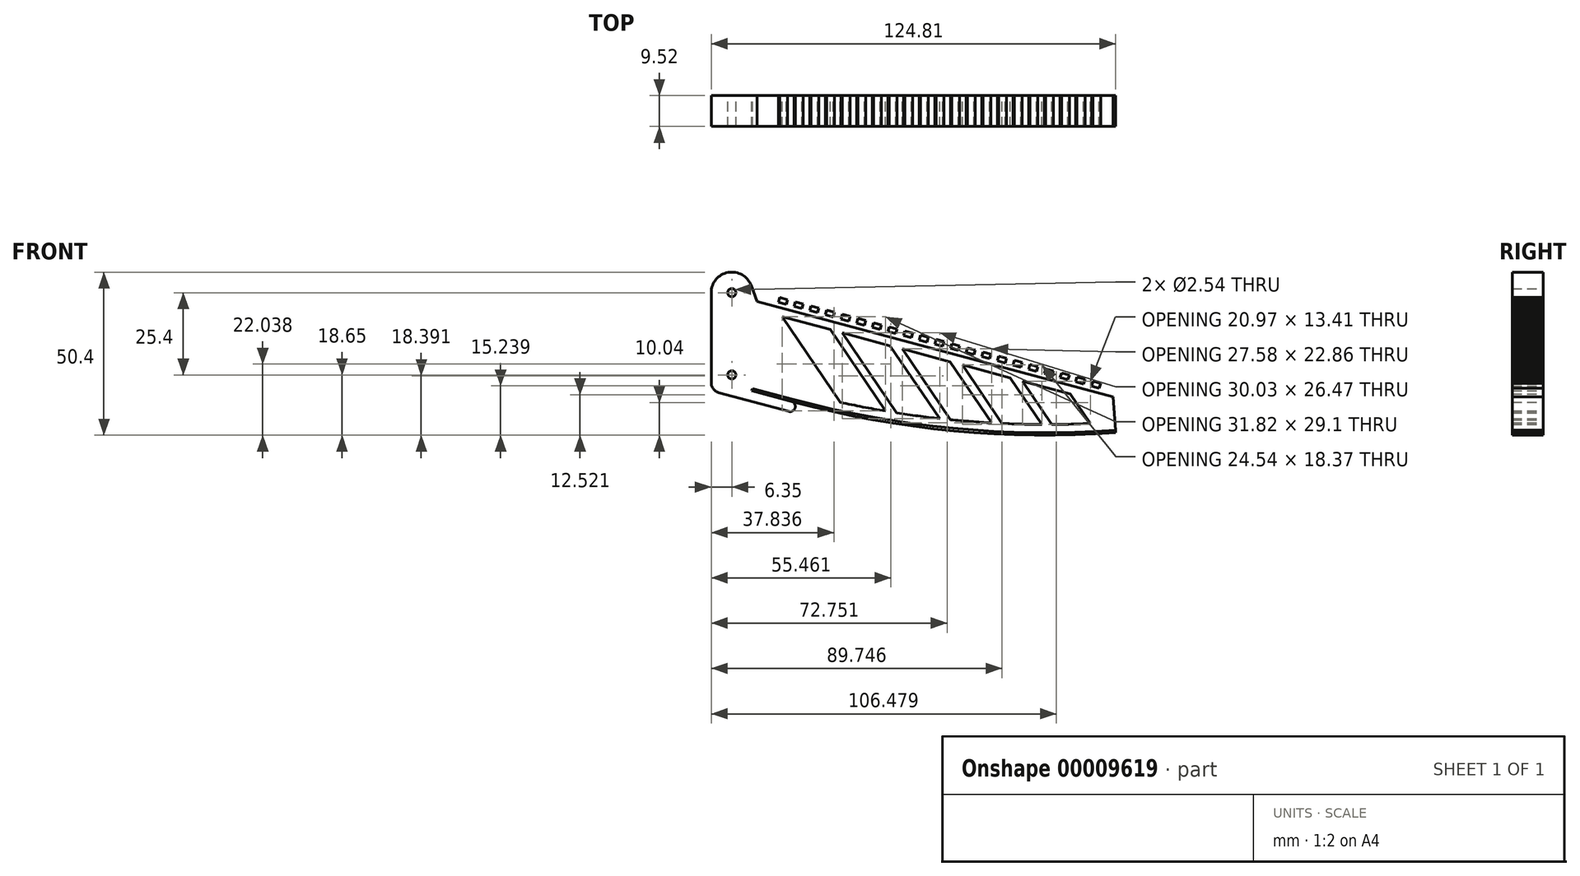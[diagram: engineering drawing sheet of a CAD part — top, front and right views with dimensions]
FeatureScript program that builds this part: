
annotation { "Feature Type Name" : "Feature", "Feature Type Description" : "" }
export const myFeature = defineFeature(function(context is Context, id is Id, definition is map)
    precondition{}
    {
        {
            var Q0;
            Q0=qCreatedBy(makeId("Front.planeOp"),FACE);
            var sketch = newSketch(context, id + "F0", { "sketchPlane" : qUnion([Q0])});
            skCircle(sketch, "E0", {"center": v(0, 0) * mm, "radius": 1.27 * mm});
            skCircle(sketch, "E1", {"center": v(0, 25.4) * mm, "radius": 1.27 * mm});
            skArc(sketch, "E2", {"start": v(5.96, 27.6) * mm, "mid": v(-1.11, 31.65) * mm, "end": v(-6.35, 25.4) * mm});
            skLineSegment(sketch, "E3", {"start": v(-6.35, 25.4) * mm, "end": v(-6.35, -2.44) * mm});
            skLineSegment(sketch, "E4", {"start": v(-4, -5.5) * mm, "end": v(17.58, -11.28) * mm});
            skLineSegment(sketch, "E5", {"start": v(19.48, -9.2) * mm, "end": v(5.96, 27.6) * mm});
            skLineSegment(sketch, "E6", {"start": v(7.14, 24.38) * mm, "end": v(117.54, -5.2) * mm});
            skLineSegment(sketch, "E7", {"start": v(117.54, -5.2) * mm, "end": v(118.46, -17.87) * mm});
            skPoint(sketch, "E8.visualSharp", {"position": v(-6.35, -4.87) * mm});
            skArc(sketch, "E8.filletArc", {"start": v(-6.35, -2.44) * mm, "mid": v(-5.7, -4.37) * mm, "end": v(-4, -5.5) * mm});
            skArc(sketch, "E9", {"start": v(19.2, -8.43) * mm, "mid": v(68.43, -17.3) * mm, "end": v(118.46, -17.87) * mm});
            skLineSegment(sketch, "E10", {"start": v(19.2, -8.43) * mm, "end": v(6.16, -4.94) * mm});
            skLineSegment(sketch, "E11", {"start": v(6.16, -4.94) * mm, "end": v(6.36, -4.2) * mm});
            skLineSegment(sketch, "E12", {"start": v(6.36, -4.2) * mm, "end": v(18.88, -7.56) * mm});
            skArc(sketch, "E13", {"start": v(18.88, -7.56) * mm, "mid": v(68.24, -16.47) * mm, "end": v(118.4, -17.1) * mm});
            skLineSegment(sketch, "E14", {"start": v(118.46, -17.87) * mm, "end": v(126.17, -17.3) * mm, "construction": true});
            skPoint(sketch, "E15.visualSharp", {"position": v(20.54, -12.08) * mm});
            skArc(sketch, "E15.filletArc", {"start": v(17.58, -11.28) * mm, "mid": v(19.16, -10.82) * mm, "end": v(19.48, -9.2) * mm});
            skLineSegment(sketch, "E16.bottom", {"start": v(9.55, 23.74) * mm, "end": v(11.97, 23.09) * mm});
            skLineSegment(sketch, "E16.top", {"start": v(9.94, 25.18) * mm, "end": v(12.36, 24.54) * mm});
            skLineSegment(sketch, "E16.left", {"start": v(9.55, 23.74) * mm, "end": v(9.94, 25.18) * mm});
            skLineSegment(sketch, "E16.right", {"start": v(11.97, 23.09) * mm, "end": v(12.36, 24.54) * mm});
            skLineSegment(sketch, "E17.1.0.0", {"start": v(14.38, 22.44) * mm, "end": v(14.77, 23.9) * mm});
            skLineSegment(sketch, "E17.1.0.1", {"start": v(16.8, 21.8) * mm, "end": v(17.19, 23.24) * mm});
            skLineSegment(sketch, "E17.1.0.2", {"start": v(14.77, 23.9) * mm, "end": v(17.19, 23.24) * mm});
            skLineSegment(sketch, "E17.1.0.3", {"start": v(14.38, 22.44) * mm, "end": v(16.8, 21.8) * mm});
            skLineSegment(sketch, "E17.2.0.0", {"start": v(19.21, 21.15) * mm, "end": v(19.6, 22.6) * mm});
            skLineSegment(sketch, "E17.2.0.1", {"start": v(21.63, 20.5) * mm, "end": v(22.02, 21.95) * mm});
            skLineSegment(sketch, "E17.2.0.2", {"start": v(19.6, 22.6) * mm, "end": v(22.02, 21.95) * mm});
            skLineSegment(sketch, "E17.2.0.3", {"start": v(19.21, 21.15) * mm, "end": v(21.63, 20.5) * mm});
            skLineSegment(sketch, "E17.3.0.0", {"start": v(24.04, 19.85) * mm, "end": v(24.43, 21.3) * mm});
            skLineSegment(sketch, "E17.3.0.1", {"start": v(26.46, 19.2) * mm, "end": v(26.85, 20.66) * mm});
            skLineSegment(sketch, "E17.3.0.2", {"start": v(24.43, 21.3) * mm, "end": v(26.85, 20.66) * mm});
            skLineSegment(sketch, "E17.3.0.3", {"start": v(24.04, 19.85) * mm, "end": v(26.46, 19.2) * mm});
            skLineSegment(sketch, "E17.4.0.0", {"start": v(28.87, 18.56) * mm, "end": v(29.26, 20) * mm});
            skLineSegment(sketch, "E17.4.0.1", {"start": v(31.29, 17.91) * mm, "end": v(31.68, 19.36) * mm});
            skLineSegment(sketch, "E17.4.0.2", {"start": v(29.26, 20) * mm, "end": v(31.68, 19.36) * mm});
            skLineSegment(sketch, "E17.4.0.3", {"start": v(28.87, 18.56) * mm, "end": v(31.29, 17.91) * mm});
            skLineSegment(sketch, "E17.5.0.0", {"start": v(33.7, 17.27) * mm, "end": v(34.1, 18.71) * mm});
            skLineSegment(sketch, "E17.5.0.1", {"start": v(36.12, 16.62) * mm, "end": v(36.5, 18.07) * mm});
            skLineSegment(sketch, "E17.5.0.2", {"start": v(34.1, 18.71) * mm, "end": v(36.5, 18.07) * mm});
            skLineSegment(sketch, "E17.5.0.3", {"start": v(33.7, 17.27) * mm, "end": v(36.12, 16.62) * mm});
            skLineSegment(sketch, "E17.6.0.0", {"start": v(38.53, 15.97) * mm, "end": v(38.92, 17.42) * mm});
            skLineSegment(sketch, "E17.6.0.1", {"start": v(40.95, 15.32) * mm, "end": v(41.33, 16.77) * mm});
            skLineSegment(sketch, "E17.6.0.2", {"start": v(38.92, 17.42) * mm, "end": v(41.33, 16.77) * mm});
            skLineSegment(sketch, "E17.6.0.3", {"start": v(38.53, 15.97) * mm, "end": v(40.95, 15.32) * mm});
            skLineSegment(sketch, "E17.7.0.0", {"start": v(43.36, 14.68) * mm, "end": v(43.75, 16.13) * mm});
            skLineSegment(sketch, "E17.7.0.1", {"start": v(45.78, 14.03) * mm, "end": v(46.16, 15.48) * mm});
            skLineSegment(sketch, "E17.7.0.2", {"start": v(43.75, 16.13) * mm, "end": v(46.16, 15.48) * mm});
            skLineSegment(sketch, "E17.7.0.3", {"start": v(43.36, 14.68) * mm, "end": v(45.78, 14.03) * mm});
            skLineSegment(sketch, "E17.8.0.0", {"start": v(48.2, 13.38) * mm, "end": v(48.58, 14.83) * mm});
            skLineSegment(sketch, "E17.8.0.1", {"start": v(50.6, 12.74) * mm, "end": v(51, 14.19) * mm});
            skLineSegment(sketch, "E17.8.0.2", {"start": v(48.58, 14.83) * mm, "end": v(51, 14.19) * mm});
            skLineSegment(sketch, "E17.8.0.3", {"start": v(48.2, 13.38) * mm, "end": v(50.6, 12.74) * mm});
            skLineSegment(sketch, "E17.9.0.0", {"start": v(53.02, 12.09) * mm, "end": v(53.4, 13.54) * mm});
            skLineSegment(sketch, "E17.9.0.1", {"start": v(55.44, 11.44) * mm, "end": v(55.82, 12.9) * mm});
            skLineSegment(sketch, "E17.9.0.2", {"start": v(53.4, 13.54) * mm, "end": v(55.82, 12.9) * mm});
            skLineSegment(sketch, "E17.9.0.3", {"start": v(53.02, 12.09) * mm, "end": v(55.44, 11.44) * mm});
            skLineSegment(sketch, "E17.10.0.0", {"start": v(57.85, 10.8) * mm, "end": v(58.24, 12.24) * mm});
            skLineSegment(sketch, "E17.10.0.1", {"start": v(60.26, 10.15) * mm, "end": v(60.65, 11.6) * mm});
            skLineSegment(sketch, "E17.10.0.2", {"start": v(58.24, 12.24) * mm, "end": v(60.65, 11.6) * mm});
            skLineSegment(sketch, "E17.10.0.3", {"start": v(57.85, 10.8) * mm, "end": v(60.26, 10.15) * mm});
            skLineSegment(sketch, "E17.11.0.0", {"start": v(62.68, 9.5) * mm, "end": v(63.07, 10.95) * mm});
            skLineSegment(sketch, "E17.11.0.1", {"start": v(65.1, 8.85) * mm, "end": v(65.48, 10.3) * mm});
            skLineSegment(sketch, "E17.11.0.2", {"start": v(63.07, 10.95) * mm, "end": v(65.48, 10.3) * mm});
            skLineSegment(sketch, "E17.11.0.3", {"start": v(62.68, 9.5) * mm, "end": v(65.1, 8.85) * mm});
            skLineSegment(sketch, "E17.12.0.0", {"start": v(67.5, 8.2) * mm, "end": v(67.9, 9.66) * mm});
            skLineSegment(sketch, "E17.12.0.1", {"start": v(69.92, 7.56) * mm, "end": v(70.31, 9) * mm});
            skLineSegment(sketch, "E17.12.0.2", {"start": v(67.9, 9.66) * mm, "end": v(70.31, 9) * mm});
            skLineSegment(sketch, "E17.12.0.3", {"start": v(67.5, 8.2) * mm, "end": v(69.92, 7.56) * mm});
            skLineSegment(sketch, "E17.13.0.0", {"start": v(72.34, 6.91) * mm, "end": v(72.73, 8.36) * mm});
            skLineSegment(sketch, "E17.13.0.1", {"start": v(74.75, 6.27) * mm, "end": v(75.14, 7.71) * mm});
            skLineSegment(sketch, "E17.13.0.2", {"start": v(72.73, 8.36) * mm, "end": v(75.14, 7.71) * mm});
            skLineSegment(sketch, "E17.13.0.3", {"start": v(72.34, 6.91) * mm, "end": v(74.75, 6.27) * mm});
            skLineSegment(sketch, "E17.14.0.0", {"start": v(77.17, 5.62) * mm, "end": v(77.56, 7.07) * mm});
            skLineSegment(sketch, "E17.14.0.1", {"start": v(79.58, 4.97) * mm, "end": v(79.97, 6.42) * mm});
            skLineSegment(sketch, "E17.14.0.2", {"start": v(77.56, 7.07) * mm, "end": v(79.97, 6.42) * mm});
            skLineSegment(sketch, "E17.14.0.3", {"start": v(77.17, 5.62) * mm, "end": v(79.58, 4.97) * mm});
            skLineSegment(sketch, "E17.15.0.0", {"start": v(82, 4.32) * mm, "end": v(82.39, 5.77) * mm});
            skLineSegment(sketch, "E17.15.0.1", {"start": v(84.41, 3.68) * mm, "end": v(84.8, 5.13) * mm});
            skLineSegment(sketch, "E17.15.0.2", {"start": v(82.39, 5.77) * mm, "end": v(84.8, 5.13) * mm});
            skLineSegment(sketch, "E17.15.0.3", {"start": v(82, 4.32) * mm, "end": v(84.41, 3.68) * mm});
            skLineSegment(sketch, "E17.16.0.0", {"start": v(86.83, 3.03) * mm, "end": v(87.22, 4.48) * mm});
            skLineSegment(sketch, "E17.16.0.1", {"start": v(89.24, 2.38) * mm, "end": v(89.63, 3.83) * mm});
            skLineSegment(sketch, "E17.16.0.2", {"start": v(87.22, 4.48) * mm, "end": v(89.63, 3.83) * mm});
            skLineSegment(sketch, "E17.16.0.3", {"start": v(86.83, 3.03) * mm, "end": v(89.24, 2.38) * mm});
            skLineSegment(sketch, "E17.17.0.0", {"start": v(91.66, 1.74) * mm, "end": v(92.05, 3.19) * mm});
            skLineSegment(sketch, "E17.17.0.1", {"start": v(94.07, 1.09) * mm, "end": v(94.46, 2.54) * mm});
            skLineSegment(sketch, "E17.17.0.2", {"start": v(92.05, 3.19) * mm, "end": v(94.46, 2.54) * mm});
            skLineSegment(sketch, "E17.17.0.3", {"start": v(91.66, 1.74) * mm, "end": v(94.07, 1.09) * mm});
            skLineSegment(sketch, "E17.18.0.0", {"start": v(96.49, 0.44) * mm, "end": v(96.88, 1.9) * mm});
            skLineSegment(sketch, "E17.18.0.1", {"start": v(98.9, -0.2) * mm, "end": v(99.3, 1.24) * mm});
            skLineSegment(sketch, "E17.18.0.2", {"start": v(96.88, 1.9) * mm, "end": v(99.3, 1.24) * mm});
            skLineSegment(sketch, "E17.18.0.3", {"start": v(96.49, 0.44) * mm, "end": v(98.9, -0.2) * mm});
            skLineSegment(sketch, "E17.19.0.0", {"start": v(101.32, -0.85) * mm, "end": v(101.7, 0.6) * mm});
            skLineSegment(sketch, "E17.19.0.1", {"start": v(103.73, -1.5) * mm, "end": v(104.12, -0.05) * mm});
            skLineSegment(sketch, "E17.19.0.2", {"start": v(101.7, 0.6) * mm, "end": v(104.12, -0.05) * mm});
            skLineSegment(sketch, "E17.19.0.3", {"start": v(101.32, -0.85) * mm, "end": v(103.73, -1.5) * mm});
            skLineSegment(sketch, "E17.direction1", {"start": v(9.55, 23.74) * mm, "end": v(14.38, 22.44) * mm, "construction": true});
            skLineSegment(sketch, "E18.0.20.0", {"start": v(106.15, -2.15) * mm, "end": v(106.53, -0.7) * mm});
            skLineSegment(sketch, "E18.3.20.0", {"start": v(108.56, -2.8) * mm, "end": v(108.95, -1.34) * mm});
            skLineSegment(sketch, "E18.6.20.0", {"start": v(106.53, -0.7) * mm, "end": v(108.95, -1.34) * mm});
            skLineSegment(sketch, "E18.9.20.0", {"start": v(106.15, -2.15) * mm, "end": v(108.56, -2.8) * mm});
            skLineSegment(sketch, "E18.0.21.0", {"start": v(110.98, -3.44) * mm, "end": v(111.36, -2) * mm});
            skLineSegment(sketch, "E18.3.21.0", {"start": v(113.4, -4.09) * mm, "end": v(113.78, -2.64) * mm});
            skLineSegment(sketch, "E18.6.21.0", {"start": v(111.36, -2) * mm, "end": v(113.78, -2.64) * mm});
            skLineSegment(sketch, "E18.9.21.0", {"start": v(110.98, -3.44) * mm, "end": v(113.4, -4.09) * mm});
            skLineSegment(sketch, "E19", {"start": v(117.66, -6.78) * mm, "end": v(7.77, 22.66) * mm});
            skArc(sketch, "E20", {"start": v(17.8, -4.63) * mm, "mid": v(67.6, -13.86) * mm, "end": v(118.22, -14.57) * mm, "construction": true});
            skLineSegment(sketch, "E21", {"start": v(110.61, -15.01) * mm, "end": v(104.41, -5.86) * mm});
            skLineSegment(sketch, "E22", {"start": v(104.41, -5.86) * mm, "end": v(89.64, -1.9) * mm});
            skLineSegment(sketch, "E23", {"start": v(89.64, -1.9) * mm, "end": v(98.73, -15.31) * mm});
            skArc(sketch, "E24", {"start": v(98.73, -15.31) * mm, "mid": v(104.68, -15.22) * mm, "end": v(110.61, -15.01) * mm});
            skLineSegment(sketch, "E25", {"start": v(95.67, -15.31) * mm, "end": v(85.9, -0.9) * mm});
            skLineSegment(sketch, "E26", {"start": v(71.13, 3.06) * mm, "end": v(83.37, -15) * mm});
            skLineSegment(sketch, "E27", {"start": v(71.13, 3.06) * mm, "end": v(85.9, -0.9) * mm});
            skLineSegment(sketch, "E28", {"start": v(80.2, -14.84) * mm, "end": v(67.38, 4.06) * mm});
            skLineSegment(sketch, "E29", {"start": v(67.38, 4.06) * mm, "end": v(52.61, 8.02) * mm});
            skLineSegment(sketch, "E30", {"start": v(52.61, 8.02) * mm, "end": v(67.43, -13.84) * mm});
            skLineSegment(sketch, "E31", {"start": v(64.13, -13.5) * mm, "end": v(48.86, 9.02) * mm});
            skLineSegment(sketch, "E32", {"start": v(48.86, 9.02) * mm, "end": v(34.1, 12.98) * mm});
            skLineSegment(sketch, "E33", {"start": v(34.1, 12.98) * mm, "end": v(50.84, -11.72) * mm});
            skLineSegment(sketch, "E34", {"start": v(47.4, -11.16) * mm, "end": v(30.34, 13.98) * mm});
            skLineSegment(sketch, "E35", {"start": v(30.34, 13.98) * mm, "end": v(15.58, 17.94) * mm});
            skLineSegment(sketch, "E36", {"start": v(15.58, 17.94) * mm, "end": v(33.5, -8.49) * mm});
            skLineSegment(sketch, "E37", {"start": v(85.9, -0.9) * mm, "end": v(89.64, -1.9) * mm, "construction": true});
            skLineSegment(sketch, "E38", {"start": v(71.13, 3.06) * mm, "end": v(67.38, 4.06) * mm, "construction": true});
            skLineSegment(sketch, "E39", {"start": v(52.61, 8.02) * mm, "end": v(48.86, 9.02) * mm, "construction": true});
            skLineSegment(sketch, "E40", {"start": v(34.1, 12.98) * mm, "end": v(30.34, 13.98) * mm, "construction": true});
            skArc(sketch, "E41", {"start": v(83.37, -15) * mm, "mid": v(89.52, -15.22) * mm, "end": v(95.67, -15.31) * mm});
            skArc(sketch, "E42", {"start": v(67.43, -13.84) * mm, "mid": v(73.8, -14.4) * mm, "end": v(80.2, -14.84) * mm});
            skArc(sketch, "E43", {"start": v(50.84, -11.72) * mm, "mid": v(57.48, -12.68) * mm, "end": v(64.13, -13.5) * mm});
            skArc(sketch, "E44", {"start": v(33.5, -8.49) * mm, "mid": v(40.43, -9.9) * mm, "end": v(47.4, -11.16) * mm});
            skArc(sketch, "E45", {"start": v(10.98, 13.93) * mm, "mid": v(1.57, 6.41) * mm, "end": v(13.6, 6.78) * mm});
            skSolve(sketch);
        }
        {
            var Q0;
            Q0=makeQuery(id+"F0.imprint","IMPRINT",FACE,{"disambiguationData":[TD([[makeQuery(id+"F0.imprint","IMPRINT",EDGE,{"derivedFrom":sQuery(id+"F0.wireOp",EDGE,"E0")}),-1.0]])]});
            var Q1;
            {var subQ0=sQuery(id+"F0.wireOp",EDGE,"E45");Q1=makeQuery(id+"F0.imprint","IMPRINT",FACE,{"disambiguationData":[TD([[makeQuery(id+"F0.imprint","IMPRINT",EDGE,{"derivedFrom":subQ0}),1.0]])]});}
            extrude(context, id + "F1", {"entities" : qUnion([Q0, Q1]), "depth" : 9.52 * mm, "symmetric" : true});
        }
        {
            var Q0;
            {var subQ22=sQuery(id+"F0.wireOp",EDGE,"E16.bottom");Q0=makeQuery(id+"F0.imprint","IMPRINT",FACE,{"disambiguationData":[TD([[makeQuery(id+"F0.imprint","IMPRINT",EDGE,{"derivedFrom":subQ22}),-1.0]])]});}
            var Q1;
            Q1=makeQuery(id+"F0.imprint","IMPRINT",FACE,{"disambiguationData":[TD([[makeQuery(id+"F0.imprint","IMPRINT",EDGE,{"derivedFrom":sQuery(id+"F0.wireOp",EDGE,"E16.bottom")}),1.0]])]});
            var Q2;
            Q2=makeQuery(id+"F0.imprint","IMPRINT",FACE,{"disambiguationData":[TD([[makeQuery(id+"F0.imprint","IMPRINT",EDGE,{"derivedFrom":sQuery(id+"F0.wireOp",EDGE,"E17.1.0.0")}),-1.0]])]});
            var Q3;
            Q3=makeQuery(id+"F0.imprint","IMPRINT",FACE,{"disambiguationData":[TD([[makeQuery(id+"F0.imprint","IMPRINT",EDGE,{"derivedFrom":sQuery(id+"F0.wireOp",EDGE,"E17.2.0.0")}),-1.0]])]});
            var Q4;
            Q4=makeQuery(id+"F0.imprint","IMPRINT",FACE,{"disambiguationData":[TD([[makeQuery(id+"F0.imprint","IMPRINT",EDGE,{"derivedFrom":sQuery(id+"F0.wireOp",EDGE,"E17.3.0.0")}),-1.0]])]});
            var Q5;
            Q5=makeQuery(id+"F0.imprint","IMPRINT",FACE,{"disambiguationData":[TD([[makeQuery(id+"F0.imprint","IMPRINT",EDGE,{"derivedFrom":sQuery(id+"F0.wireOp",EDGE,"E17.4.0.0")}),-1.0]])]});
            var Q6;
            Q6=makeQuery(id+"F0.imprint","IMPRINT",FACE,{"disambiguationData":[TD([[makeQuery(id+"F0.imprint","IMPRINT",EDGE,{"derivedFrom":sQuery(id+"F0.wireOp",EDGE,"E17.5.0.0")}),-1.0]])]});
            var Q7;
            Q7=makeQuery(id+"F0.imprint","IMPRINT",FACE,{"disambiguationData":[TD([[makeQuery(id+"F0.imprint","IMPRINT",EDGE,{"derivedFrom":sQuery(id+"F0.wireOp",EDGE,"E17.6.0.0")}),-1.0]])]});
            var Q8;
            Q8=makeQuery(id+"F0.imprint","IMPRINT",FACE,{"disambiguationData":[TD([[makeQuery(id+"F0.imprint","IMPRINT",EDGE,{"derivedFrom":sQuery(id+"F0.wireOp",EDGE,"E17.7.0.0")}),-1.0]])]});
            var Q9;
            Q9=makeQuery(id+"F0.imprint","IMPRINT",FACE,{"disambiguationData":[TD([[makeQuery(id+"F0.imprint","IMPRINT",EDGE,{"derivedFrom":sQuery(id+"F0.wireOp",EDGE,"E17.8.0.0")}),-1.0]])]});
            var Q10;
            Q10=makeQuery(id+"F0.imprint","IMPRINT",FACE,{"disambiguationData":[TD([[makeQuery(id+"F0.imprint","IMPRINT",EDGE,{"derivedFrom":sQuery(id+"F0.wireOp",EDGE,"E17.9.0.0")}),-1.0]])]});
            var Q11;
            Q11=makeQuery(id+"F0.imprint","IMPRINT",FACE,{"disambiguationData":[TD([[makeQuery(id+"F0.imprint","IMPRINT",EDGE,{"derivedFrom":sQuery(id+"F0.wireOp",EDGE,"E17.10.0.0")}),-1.0]])]});
            var Q12;
            Q12=makeQuery(id+"F0.imprint","IMPRINT",FACE,{"disambiguationData":[TD([[makeQuery(id+"F0.imprint","IMPRINT",EDGE,{"derivedFrom":sQuery(id+"F0.wireOp",EDGE,"E17.11.0.0")}),-1.0]])]});
            var Q13;
            Q13=makeQuery(id+"F0.imprint","IMPRINT",FACE,{"disambiguationData":[TD([[makeQuery(id+"F0.imprint","IMPRINT",EDGE,{"derivedFrom":sQuery(id+"F0.wireOp",EDGE,"E17.12.0.0")}),-1.0]])]});
            var Q14;
            Q14=makeQuery(id+"F0.imprint","IMPRINT",FACE,{"disambiguationData":[TD([[makeQuery(id+"F0.imprint","IMPRINT",EDGE,{"derivedFrom":sQuery(id+"F0.wireOp",EDGE,"E17.13.0.0")}),-1.0]])]});
            var Q15;
            Q15=makeQuery(id+"F0.imprint","IMPRINT",FACE,{"disambiguationData":[TD([[makeQuery(id+"F0.imprint","IMPRINT",EDGE,{"derivedFrom":sQuery(id+"F0.wireOp",EDGE,"E17.14.0.0")}),-1.0]])]});
            var Q16;
            Q16=makeQuery(id+"F0.imprint","IMPRINT",FACE,{"disambiguationData":[TD([[makeQuery(id+"F0.imprint","IMPRINT",EDGE,{"derivedFrom":sQuery(id+"F0.wireOp",EDGE,"E17.15.0.0")}),-1.0]])]});
            var Q17;
            Q17=makeQuery(id+"F0.imprint","IMPRINT",FACE,{"disambiguationData":[TD([[makeQuery(id+"F0.imprint","IMPRINT",EDGE,{"derivedFrom":sQuery(id+"F0.wireOp",EDGE,"E17.16.0.0")}),-1.0]])]});
            var Q18;
            Q18=makeQuery(id+"F0.imprint","IMPRINT",FACE,{"disambiguationData":[TD([[makeQuery(id+"F0.imprint","IMPRINT",EDGE,{"derivedFrom":sQuery(id+"F0.wireOp",EDGE,"E17.17.0.0")}),-1.0]])]});
            var Q19;
            Q19=makeQuery(id+"F0.imprint","IMPRINT",FACE,{"disambiguationData":[TD([[makeQuery(id+"F0.imprint","IMPRINT",EDGE,{"derivedFrom":sQuery(id+"F0.wireOp",EDGE,"E17.18.0.0")}),-1.0]])]});
            var Q20;
            Q20=makeQuery(id+"F0.imprint","IMPRINT",FACE,{"disambiguationData":[TD([[makeQuery(id+"F0.imprint","IMPRINT",EDGE,{"derivedFrom":sQuery(id+"F0.wireOp",EDGE,"E18.0.20.0")}),-1.0]])]});
            var Q21;
            Q21=makeQuery(id+"F0.imprint","IMPRINT",FACE,{"disambiguationData":[TD([[makeQuery(id+"F0.imprint","IMPRINT",EDGE,{"derivedFrom":sQuery(id+"F0.wireOp",EDGE,"E18.0.21.0")}),-1.0]])]});
            var Q22;
            Q22=makeQuery(id+"F0.imprint","IMPRINT",FACE,{"disambiguationData":[TD([[makeQuery(id+"F0.imprint","IMPRINT",EDGE,{"derivedFrom":sQuery(id+"F0.wireOp",EDGE,"E17.19.0.0")}),-1.0]])]});
            extrude(context, id + "F2", {"entities" : qUnion([Q0, Q1, Q2, Q3, Q4, Q5, Q6, Q7, Q8, Q9, Q10, Q11, Q12, Q13, Q14, Q15, Q16, Q17, Q18, Q19, Q20, Q21, Q22]), "depth" : 9.52 * mm, "symmetric" : true});
        }
        {
            var Q0;
            {var subQ5=sQuery(id+"F0.wireOp",EDGE,"E13");Q0=makeQuery(id+"F0.imprint","IMPRINT",FACE,{"disambiguationData":[TD([[makeQuery(id+"F0.imprint","IMPRINT",EDGE,{"derivedFrom":subQ5}),1.0]])]});}
            extrude(context, id + "F3", {"entities" : qUnion([Q0]), "depth" : 9.52 * mm, "symmetric" : true});
        }
        {
            var Q0;
            {var subQ1=sQuery(id+"F0.wireOp",EDGE,"E9");Q0=makeQuery(id+"F0.imprint","IMPRINT",FACE,{"disambiguationData":[TD([[makeQuery(id+"F0.imprint","IMPRINT",EDGE,{"derivedFrom":subQ1}),1.0]])]});}
            var Q1;
            {var subQ1=sQuery(id+"F0.wireOp",EDGE,"E10");Q1=makeQuery(id+"F0.imprint","IMPRINT",FACE,{"disambiguationData":[TD([[makeQuery(id+"F0.imprint","IMPRINT",EDGE,{"derivedFrom":subQ1}),-1.0]])]});}
            extrude(context, id + "F4", {"entities" : qUnion([Q0, Q1]), "depth" : 9.52 * mm, "symmetric" : true});
        }
        {
            var Q0;
            {var subQ0=sQuery(id+"F0.wireOp",EDGE,"E45");Q0=makeQuery(id+"F0.imprint","IMPRINT",FACE,{"disambiguationData":[TD([[makeQuery(id+"F0.imprint","IMPRINT",EDGE,{"derivedFrom":subQ0}),1.0]])]});}
            extrude(context, id + "F5", {"entities" : qUnion([Q0]), "operationType" : NewBodyOperationType.REMOVE, "oppositeDirection" : true, "depth" : 6.35 * mm, "symmetric" : true});
        }
        {
            var Q0;
            {var subQ0=sQuery(id+"F0.wireOp",EDGE,"E45");Q0=makeQuery(id+"F0.imprint","IMPRINT",FACE,{"disambiguationData":[TD([[makeQuery(id+"F0.imprint","IMPRINT",EDGE,{"derivedFrom":subQ0}),1.0]])]});}
            extrude(context, id + "F6", {"entities" : qUnion([Q0]), "operationType" : NewBodyOperationType.ADD, "depth" : 6.35 * mm, "symmetric" : true});
        }
    });
